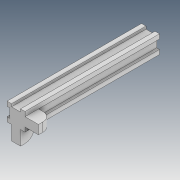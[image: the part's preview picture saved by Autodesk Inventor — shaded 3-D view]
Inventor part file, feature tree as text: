
AUTODESK INVENTOR PART (.ipt)
format: ipt  version: 2021 (Build 250183000, 183)  size: 143,360 bytes
history: native  units: mm
features: extrude x2, sketch x2, other x1, fillet x1
ambient origin geometry x8: Origin, YZ Plane, XZ Plane, XY Plane, X Axis, Y Axis, Z Axis, Center Point
bodies: Body1 (feature_tree)
feature tree (6):
  other  "Sólido1"
  extrude  "Extrusão1"  Depth=5.0mm
  extrude  "Extrusão2"  Depth=10.0mm
  fillet  "Arredondamento1"  Radius=3.0mm
  sketch  "Esboço1"  dims[d4=5.0mm d5=5.0mm]
  sketch  "Esboço5"  dims[d6=3.0mm d7=10.0mm d8=3.0mm d9=5.0mm d10=5.0mm d11=3.0mm d12=10.0mm d13=5.0mm d14=5.0mm d15=3.0mm d16=10.0mm d17=3.0mm d18=5.0mm d19=3.0mm d20=10.0mm d21=150.0mm d22=0.0mm d23=15.0mm d24=0.0mm d25=10.0mm]
